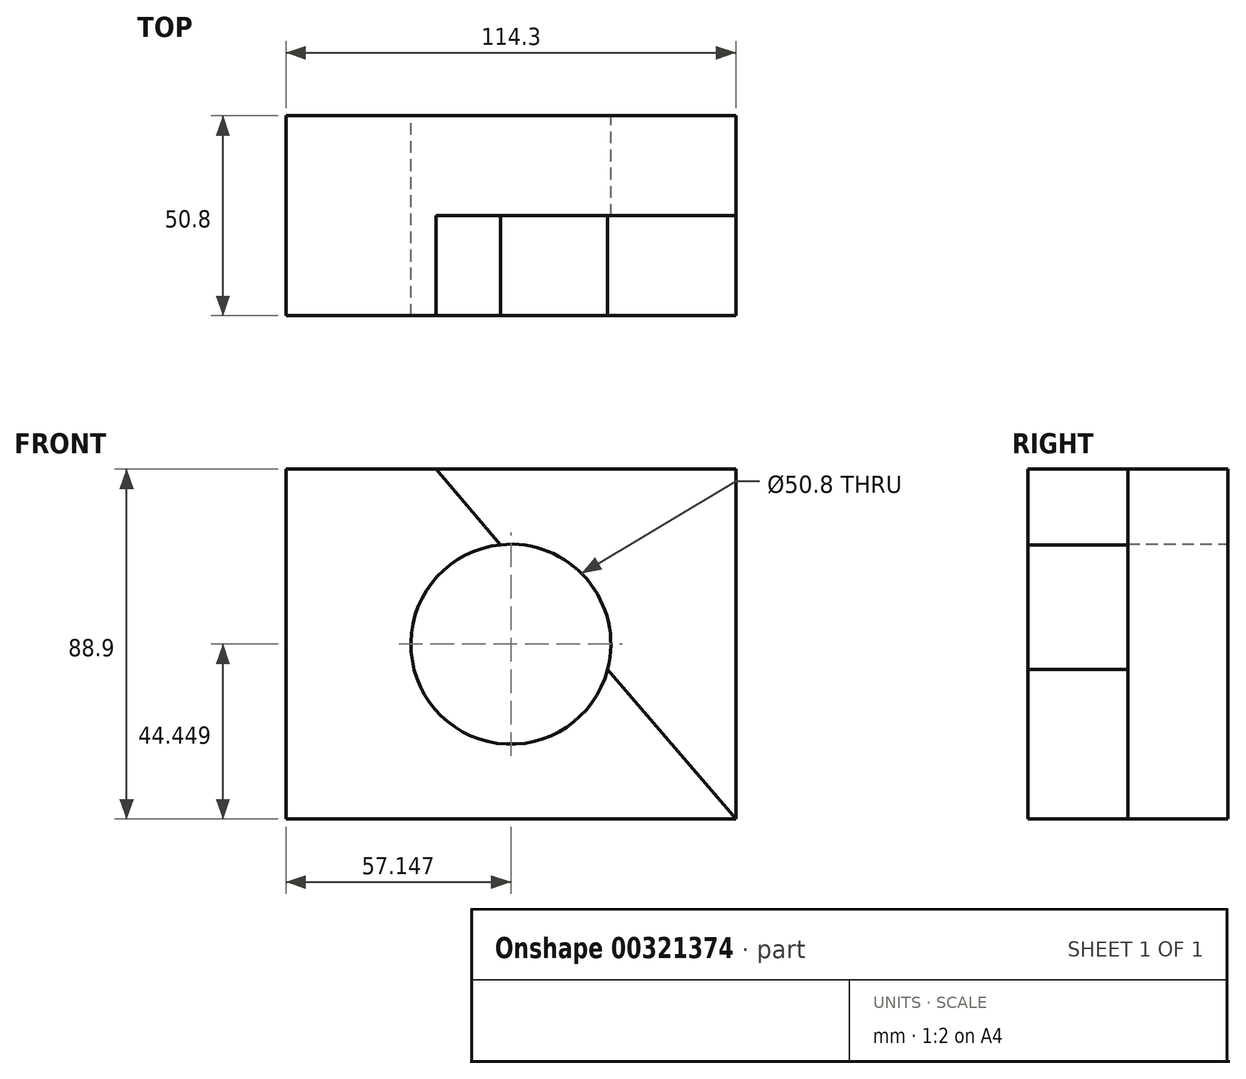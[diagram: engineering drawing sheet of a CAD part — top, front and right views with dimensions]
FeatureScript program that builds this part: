
annotation { "Feature Type Name" : "Feature", "Feature Type Description" : "" }
export const myFeature = defineFeature(function(context is Context, id is Id, definition is map)
    precondition{}
    {
        {
            var Q0;
            Q0=qCreatedBy(makeId("Front.planeOp"),FACE);
            var sketch = newSketch(context, id + "F0", { "sketchPlane" : qUnion([Q0])});
            skLineSegment(sketch, "E0.bottom", {"start": v(-54.75, -13.93) * mm, "end": v(59.55, -13.93) * mm});
            skLineSegment(sketch, "E0.top", {"start": v(-54.75, -102.83) * mm, "end": v(59.55, -102.83) * mm});
            skLineSegment(sketch, "E0.left", {"start": v(-54.75, -13.93) * mm, "end": v(-54.75, -102.83) * mm});
            skLineSegment(sketch, "E0.right", {"start": v(59.55, -13.93) * mm, "end": v(59.55, -102.83) * mm});
            skLineSegment(sketch, "E1", {"start": v(-54.75, -13.93) * mm, "end": v(-16.65, -13.93) * mm});
            skCircle(sketch, "E2", {"center": v(2.4, -58.38) * mm, "radius": 25.4 * mm});
            skPoint(sketch, "E2.centerSnap0", {"position": v(2.4, -102.83) * mm});
            skPoint(sketch, "E2.centerSnap1", {"position": v(-54.75, -58.38) * mm});
            skSolve(sketch);
        }
        {
            var Q0;
            Q0=makeQuery(id+"F0.imprint","IMPRINT",FACE,{"disambiguationData":[TD([[makeQuery(id+"F0.imprint","IMPRINT",EDGE,{"derivedFrom":sQuery(id+"F0.wireOp",EDGE,"E0.bottom")}),-1.0]])]});
            extrude(context, id + "F1", {"entities" : qUnion([Q0]), "depth" : 50.8 * mm});
        }
        {
            var Q0;
            Q0=makeQuery(id+"F1.opExtrude","CAP_FACE",FACE,{"disambiguationData":[OSD([sQuery(id+"F0.wireOp",EDGE,"E0.bottom"),sQuery(id+"F0.wireOp",EDGE,"E0.top"),sQuery(id+"F0.wireOp",EDGE,"E0.left"),sQuery(id+"F0.wireOp",EDGE,"E0.right"),sQuery(id+"F0.wireOp",EDGE,"E1"),sQuery(id+"F0.wireOp",EDGE,"E2")])],"isStart":false});
            var sketch = newSketch(context, id + "F2", { "sketchPlane" : qUnion([Q0])});
            skLineSegment(sketch, "E3", {"start": v(-54.75, -13.93) * mm, "end": v(-16.65, -13.93) * mm});
            skLineSegment(sketch, "E4", {"start": v(-16.65, -13.93) * mm, "end": v(59.55, -102.83) * mm});
            skSolve(sketch);
        }
        {
            var Q0;
            Q0 = qSketchRegion(id + "F2", true);
            var Q1;
            {var subQ0=makeQuery(id+"F1.opExtrude","CAP_EDGE",EDGE,{"disambiguationData":[OSD([sQuery(id+"F0.wireOp",EDGE,"E0.right")])],"isStart":false});Q1=makeQuery(id+"F2.imprint","IMPRINT",FACE,{"disambiguationData":[TD([[makeQuery(id+"F2.imprint","IMPRINT",EDGE,{"derivedFrom":subQ0}),-1.0]])]});}
            extrude(context, id + "F3", {"entities" : qUnion([Q0, Q1]), "operationType" : NewBodyOperationType.REMOVE, "oppositeDirection" : true, "depth" : 25.4 * mm});
        }
    });
